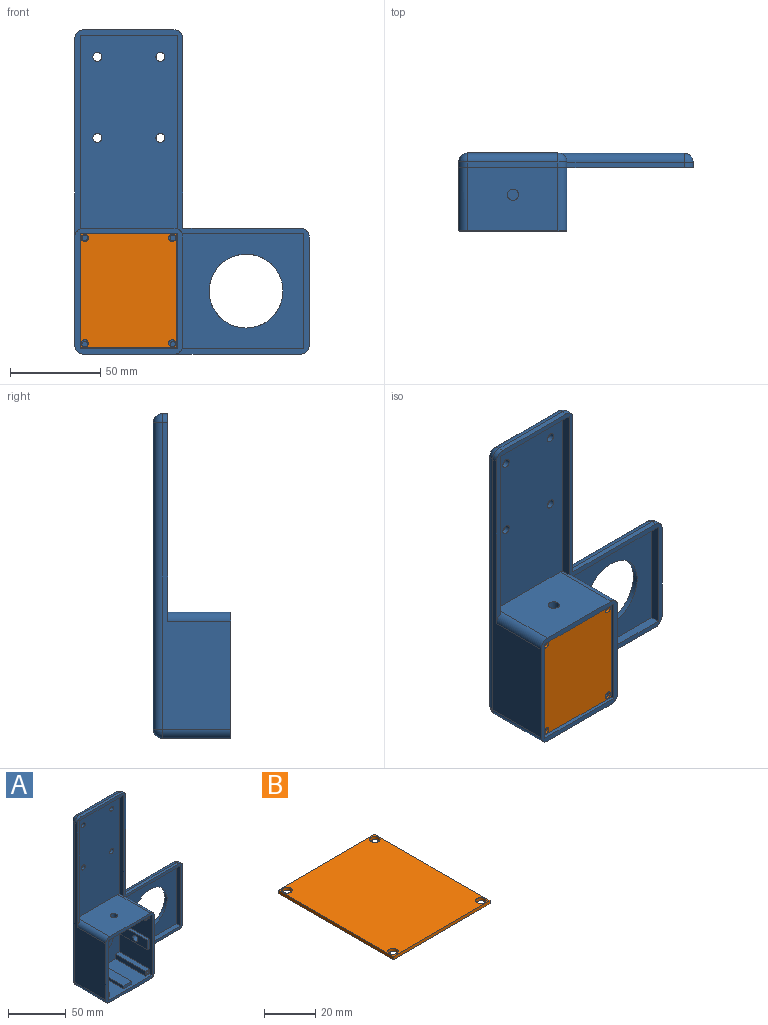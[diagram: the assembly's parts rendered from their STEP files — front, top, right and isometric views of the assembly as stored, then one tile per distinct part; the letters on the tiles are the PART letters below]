
ASSEMBLY  parts=2 mates=1
PART A: 89 faces, bbox 130x43x180 mm
  f0: plane 107.42x54mm, normal (0,-1,0), area 5700mm2, adj f13,f14,f15,f16,f21,f66,f67,f68
  f1: plane 65x3mm, normal (0,0,1), area 195mm2, adj f9,f69,f75,f84
  f2: plane 60x40mm, normal (1,0,0), area 2370.3mm2, adj f3,f22,f64,f87,f88
  f3: plane 67.42x64mm, normal (0,-1,0), area 2968.3mm2, adj f2,f60,f61,f62,f63,f87,f88
  f4: plane 64x54mm, normal (0,-1,0), area 2218.1mm2, adj f5,f6,f7,f8,f19,f23,f24,f26
  f5: plane 64x40mm, normal (1,0,0), area 1820mm2, adj f4,f7,f8,f22,f27,f28,f30,f31
  f6: plane 64x40mm, normal (-1,0,0), area 1820mm2, adj f4,f7,f8,f22,f24,f25,f33,f34
  f7: plane 54x40mm, normal (0,0,1), area 1420mm2, adj f4,f5,f6,f22,f29,f31,f32,f34
  f8: plane 54x40mm, normal (0,0,-1), area 1420mm2, adj f4,f5,f6,f22,f23,f25,f26,f28
  f9: plane 105x3mm, normal (1,0,0), area 315mm2, adj f1,f69,f74,f76
  f10: plane 50x3mm, normal (0,0,1), area 150mm2, adj f69,f72,f76,f80
  f11: plane 170x38mm, normal (-1,0,0), area 2610mm2, adj f22,f69,f70,f78,f80,f86
  f12: cylinder r=12.75mm len=25.5mm, axis (0,-1,0), area 448.6mm2, adj f18,f20
  f13: cylinder r=2.5mm len=5mm, axis (0,-1,0), area 47.1mm2, adj f0,f18
  f14: cylinder r=2.5mm len=5mm, axis (0,-1,0), area 47.1mm2, adj f0,f18
  f15: cylinder r=2.5mm len=5mm, axis (0,-1,0), area 47.1mm2, adj f0,f18
  f16: cylinder r=2.5mm len=5mm, axis (0,-1,0), area 47.1mm2, adj f0,f18
  f17: plane 120x38mm, normal (0,0,-1), area 2110mm2, adj f22,f69,f71,f78,f82,f88
  f18: plane 170x120mm, normal (0,1,0), area 10790.5mm2, adj f12,f13,f14,f15,f16,f60,f70,f71
  f19: cylinder r=18mm len=36mm, axis (0,1,0), area 294.1mm2, adj f4,f20
  f20: plane 36x36mm, normal (0,-1,0), area 507.2mm2, adj f12,f19
  f21: plane 50x40mm, normal (0,0,1), area 1969.8mm2, adj f0,f22,f65,f86,f87
  f22: plane 70x60mm, normal (0,-1,0), area 722.5mm2, adj f2,f5,f6,f7,f8,f11,f17,f21
  f23: plane 37x5mm, normal (-1,0,0), area 185mm2, adj f4,f8,f24,f25
  f24: plane 37x5mm, normal (0,0,-1), area 185mm2, adj f4,f6,f23,f25
  f25: plane 5x5mm, normal (0,-1,0), area 17mm2, adj f6,f8,f23,f24,f57
  f26: plane 37x5mm, normal (1,0,0), area 185mm2, adj f4,f8,f27,f28
  f27: plane 37x5mm, normal (0,0,-1), area 185mm2, adj f4,f5,f26,f28
  f28: plane 5x5mm, normal (0,-1,0), area 17mm2, adj f5,f8,f26,f27,f55
  f29: plane 37x5mm, normal (1,0,0), area 185mm2, adj f4,f7,f30,f31
  f30: plane 37x5mm, normal (0,0,1), area 185mm2, adj f4,f5,f29,f31
  f31: plane 5x5mm, normal (0,-1,0), area 17mm2, adj f5,f7,f29,f30,f53
  f32: plane 37x5mm, normal (-1,0,0), area 185mm2, adj f4,f7,f33,f34
  f33: plane 37x5mm, normal (0,0,1), area 185mm2, adj f4,f6,f32,f34
  f34: plane 5x5mm, normal (0,-1,0), area 17mm2, adj f6,f7,f32,f33,f51
  f35: plane 37x3mm, normal (1,0,0), area 111mm2, adj f4,f8,f37,f38
  f36: plane 37x3mm, normal (-1,0,0), area 111mm2, adj f4,f8,f37,f38
  f37: plane 37x10mm, normal (0,0,-1), area 339.8mm2, adj f4,f35,f36,f38,f65
  f38: plane 10x3mm, normal (0,-1,0), area 30mm2, adj f8,f35,f36,f37
  f39: plane 37x3mm, normal (1,0,0), area 111mm2, adj f4,f7,f40,f42
  f40: plane 37x10mm, normal (0,0,1), area 370mm2, adj f4,f39,f41,f42
  f41: plane 37x3mm, normal (-1,0,0), area 111mm2, adj f4,f7,f40,f42
  f42: plane 10x3mm, normal (0,-1,0), area 30mm2, adj f7,f39,f40,f41
  f43: plane 37x3mm, normal (0,0,-1), area 111mm2, adj f4,f6,f45,f46
  f44: plane 37x3mm, normal (0,0,1), area 111mm2, adj f4,f6,f45,f46
  f45: plane 37x10mm, normal (-1,0,0), area 340.3mm2, adj f4,f43,f44,f46,f64
  f46: plane 10x3mm, normal (0,-1,0), area 30mm2, adj f6,f43,f44,f45
  f47: plane 37x3mm, normal (0,0,-1), area 111mm2, adj f4,f5,f48,f50
  f48: plane 37x10mm, normal (1,0,0), area 370mm2, adj f4,f47,f49,f50
  f49: plane 37x3mm, normal (0,0,1), area 111mm2, adj f4,f5,f48,f50
  f50: plane 10x3mm, normal (0,-1,0), area 30mm2, adj f5,f47,f48,f49
  f51: cylinder r=1.6mm len=28mm, axis (0,-1,0), area 281.5mm2, adj f34,f52
  f52: plane 3.2x3.2mm, normal (0,-1,0), area 8mm2, adj f51
  f53: cylinder r=1.6mm len=28mm, axis (0,-1,0), area 281.5mm2, adj f31,f54
  f54: plane 3.2x3.2mm, normal (0,-1,0), area 8mm2, adj f53
  f55: cylinder r=1.6mm len=28mm, axis (0,-1,0), area 281.5mm2, adj f28,f56
  f56: plane 3.2x3.2mm, normal (0,-1,0), area 8mm2, adj f55
  f57: cylinder r=1.6mm len=28mm, axis (0,-1,0), area 281.5mm2, adj f25,f58
  f58: plane 3.2x3.2mm, normal (0,-1,0), area 8mm2, adj f57
  f59: plane 60x3mm, normal (1,0,0), area 180mm2, adj f69,f73,f82,f84
  f60: cylinder r=20.5mm len=41mm, axis (0,-1,0), area 386.4mm2, adj f3,f18
  f61: plane 67.42x5mm, normal (0,0,1), area 337.1mm2, adj f3,f63,f69,f88
  f62: plane 67.42x5mm, normal (0,0,-1), area 337.1mm2, adj f3,f63,f69,f87
  f63: plane 64x5mm, normal (-1,0,0), area 320mm2, adj f3,f61,f62,f69
  f64: cylinder r=3.08mm len=6.15mm, axis (1,0,0), area 115.9mm2, adj f2,f45
  f65: cylinder r=3.1mm len=6.2mm, axis (0,0,1), area 116.9mm2, adj f21,f37
  f66: plane 107.42x5mm, normal (1,0,0), area 537.1mm2, adj f0,f67,f69,f86
  f67: plane 54x5mm, normal (0,0,-1), area 270mm2, adj f0,f66,f68,f69
  f68: plane 107.42x5mm, normal (-1,0,0), area 537.1mm2, adj f0,f67,f69,f87
  f69: plane 180x130mm, normal (0,-1,0), area 1427.5mm2, adj f1,f9,f10,f11,f17,f59,f61,f62
  f70: cylinder r=5mm len=170mm, axis (0,0,1), area 1335.2mm2, adj f11,f18,f79,f81
  f71: cylinder r=5mm len=120mm, axis (-1,0,0), area 942.5mm2, adj f17,f18,f79,f83
  f72: cylinder r=5mm len=50mm, axis (1,0,0), area 392.7mm2, adj f10,f18,f77,f81
  f73: cylinder r=5mm len=60mm, axis (0,0,-1), area 471.2mm2, adj f18,f59,f83,f85
  f74: cylinder r=5mm len=110mm, axis (0,0,-1), area 838.9mm2, adj f9,f18,f75,f77
  f75: cylinder r=5mm len=70mm, axis (1,0,0), area 524.8mm2, adj f1,f18,f74,f85
  f76: cylinder r=5mm len=5mm, axis (0,-1,0), area 23.6mm2, adj f9,f10,f69,f77
  f77: sphere r=5mm, area 39.3mm2, adj f72,f74,f76
  f78: cylinder r=5mm len=38mm, axis (0,-1,0), area 298.5mm2, adj f11,f17,f22,f79
  f79: sphere r=5mm, area 39.3mm2, adj f70,f71,f78
  f80: cylinder r=5mm len=5mm, axis (0,1,0), area 23.6mm2, adj f10,f11,f69,f81
  f81: sphere r=5mm, area 39.3mm2, adj f70,f72,f80
  f82: cylinder r=5mm len=5mm, axis (0,1,0), area 23.6mm2, adj f17,f59,f69,f83
  f83: sphere r=5mm, area 39.3mm2, adj f71,f73,f82
  f84: cylinder r=5mm len=5mm, axis (0,-1,0), area 23.6mm2, adj f1,f59,f69,f85
  f85: sphere r=5mm, area 39.3mm2, adj f73,f75,f84
  f86: cylinder r=5mm len=40mm, axis (0,-1,0), area 285.2mm2, adj f0,f11,f21,f22,f66,f69
  f87: cylinder r=5mm len=40mm, axis (0,1,0), area 295.5mm2, adj f0,f2,f3,f21,f22,f62,f68,f69
  f88: cylinder r=5mm len=40mm, axis (0,1,0), area 285.2mm2, adj f2,f3,f17,f22,f61,f69
PART B: 10 faces, bbox 53.5x63.5x1.5 mm
  f0: plane 63.5x1.5mm, normal (-1,0,0), area 95.2mm2, adj f1,f6,f8,f9
  f1: plane 53.5x1.5mm, normal (0,-1,0), area 80.2mm2, adj f0,f2,f8,f9
  f2: plane 63.5x1.5mm, normal (1,0,0), area 95.2mm2, adj f1,f6,f8,f9
  f3: cylinder r=2mm len=4mm, axis (0,0,-1), area 18.8mm2, adj f8,f9
  f4: cylinder r=2mm len=4mm, axis (0,0,-1), area 18.8mm2, adj f8,f9
  f5: cylinder r=2mm len=4mm, axis (0,0,-1), area 18.8mm2, adj f8,f9
  f6: plane 53.5x1.5mm, normal (0,1,0), area 80.3mm2, adj f0,f2,f8,f9
  f7: cylinder r=2mm len=4mm, axis (0,0,-1), area 18.8mm2, adj f8,f9
  f8: plane 63.5x53.5mm, normal (0,0,1), area 3347mm2, adj f0,f1,f2,f3,f4,f5,f6,f7
  f9: plane 63.5x53.5mm, normal (0,0,-1), area 3347mm2, adj f0,f1,f2,f3,f4,f5,f6,f7
PLACE A t=(60.55,-101.26,-22.81)mm
PLACE B rot(axis=(1,0,0),90deg) t=(33.55,-138.26,-109.31)mm
MATE slider A.f55 <-> B.f5  axis (0,-1,0) through (36.05,-138.26,-48.31)mm
